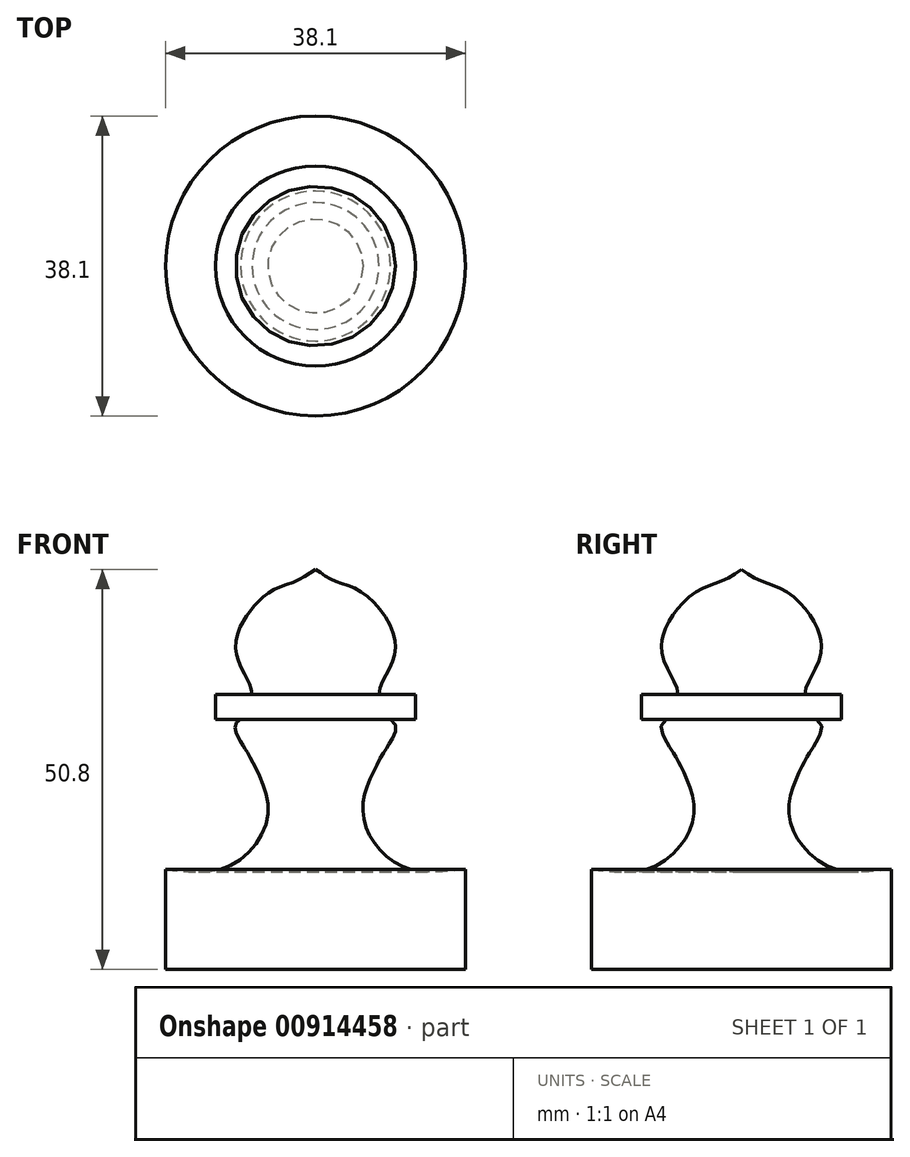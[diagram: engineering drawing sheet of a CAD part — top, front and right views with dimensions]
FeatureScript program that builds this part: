
annotation { "Feature Type Name" : "Feature", "Feature Type Description" : "" }
export const myFeature = defineFeature(function(context is Context, id is Id, definition is map)
    precondition{}
    {
        {
            var Q0;
            Q0=qCreatedBy(makeId("Front.planeOp"),FACE);
            var sketch = newSketch(context, id + "F0", { "sketchPlane" : qUnion([Q0])});
            skLineSegment(sketch, "E0", {"start": v(0, 50.8) * mm, "end": v(0, 0) * mm});
            skLineSegment(sketch, "E1", {"start": v(0, 0) * mm, "end": v(19.05, 0) * mm});
            skLineSegment(sketch, "E2", {"start": v(0, 31.75) * mm, "end": v(16.9, 31.75) * mm, "construction": true});
            skLineSegment(sketch, "E3", {"start": v(19.05, 0) * mm, "end": v(19.05, 12.7) * mm});
            skFitSpline(sketch, "E4", {"points": [v(19.05, 12.7) * mm, v(12.13, 12.7) * mm, v(7.72, 15.75) * mm, v(6, 20.15) * mm, v(6.99, 24.31) * mm, v(8.57, 27.4) * mm, v(9.68, 29.2) * mm, v(9.53, 31.75) * mm], "startDerivative": vector(-42.46, -5) * mm, "endDerivative": vector(-30.31, 14.49) * mm});
            skLineSegment(sketch, "E5.bottom", {"start": v(0, 31.75) * mm, "end": v(12.7, 31.75) * mm});
            skLineSegment(sketch, "E5.top", {"start": v(0, 34.92) * mm, "end": v(12.7, 34.92) * mm});
            skLineSegment(sketch, "E5.left", {"start": v(0, 31.75) * mm, "end": v(0, 34.92) * mm});
            skLineSegment(sketch, "E5.right", {"start": v(12.7, 31.75) * mm, "end": v(12.7, 34.92) * mm});
            skFitSpline(sketch, "E6", {"points": [v(8.06, 34.92) * mm, v(9.65, 38.74) * mm, v(9.8, 42.96) * mm, v(5.87, 47.9) * mm, v(2.44, 49.36) * mm, v(0, 50.8) * mm], "startDerivative": vector(0.32, 18.97) * mm, "endDerivative": vector(-13.62, 8.89) * mm});
            skSolve(sketch);
        }
        {
            var Q0;
            {var subQ7=sQuery(id+"F0.wireOp",EDGE,"E5.right");Q0=makeQuery(id+"F0.imprint","IMPRINT",FACE,{"disambiguationData":[TD([[makeQuery(id+"F0.imprint","IMPRINT",EDGE,{"derivedFrom":subQ7}),1.0]])]});}
            var Q1;
            {var subQ3=sQuery(id+"F0.wireOp",EDGE,"E6");Q1=makeQuery(id+"F0.imprint","IMPRINT",FACE,{"disambiguationData":[TD([[makeQuery(id+"F0.imprint","IMPRINT",EDGE,{"derivedFrom":subQ3}),1.0]])]});}
            var Q2;
            {var subQ0=sQuery(id+"F0.wireOp",EDGE,"E1");Q2=makeQuery(id+"F0.imprint","IMPRINT",FACE,{"disambiguationData":[TD([[makeQuery(id+"F0.imprint","IMPRINT",EDGE,{"derivedFrom":subQ0}),1.0]])]});}
            var Q3;
            Q3=sQuery(id+"F0.wireOp",EDGE,"E0");
            revolve(context, id + "F1", {"surfaceOperationType" : NewSurfaceOperationType.NEW, "entities" : qUnion([Q0, Q1, Q2]), "axis" : qUnion([Q3]), "revolveType" : RevolveType.FULL});
        }
    });
